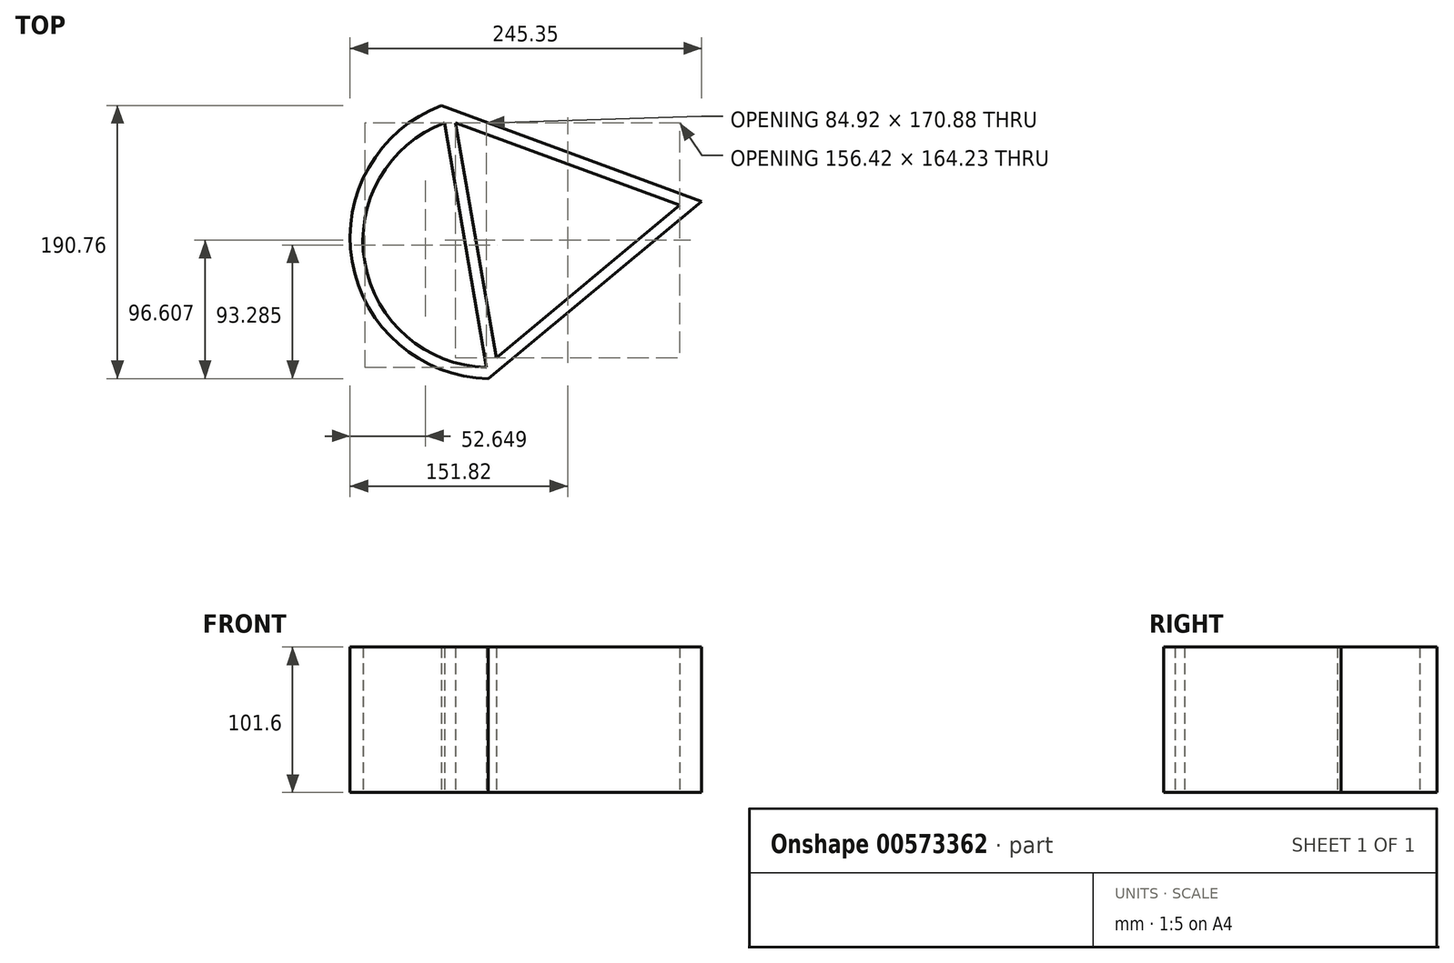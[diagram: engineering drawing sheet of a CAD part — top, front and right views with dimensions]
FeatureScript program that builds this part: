
annotation { "Feature Type Name" : "Feature", "Feature Type Description" : "" }
export const myFeature = defineFeature(function(context is Context, id is Id, definition is map)
    precondition{}
    {
        {
            var Q0;
            Q0=qCreatedBy(makeId("Top.planeOp"),FACE);
            var sketch = newSketch(context, id + "F0", { "sketchPlane" : qUnion([Q0])});
            skCircle(sketch, "E0.cCircle", {"center": v(0, 0) * mm, "radius": 55.87 * mm, "construction": true});
            skLineSegment(sketch, "E0.0", {"start": v(110.14, 18.83) * mm, "end": v(-38.76, -104.8) * mm});
            skLineSegment(sketch, "E0.1", {"start": v(-38.76, -104.8) * mm, "end": v(-71.38, 85.96) * mm});
            skLineSegment(sketch, "E0.2", {"start": v(-71.38, 85.96) * mm, "end": v(110.14, 18.83) * mm});
            skPoint(sketch, "E0.0.midPoint", {"position": v(35.69, -42.98) * mm});
            skCircle(sketch, "E1.cCircle", {"center": v(0, 0) * mm, "radius": 48.11 * mm, "construction": true});
            skLineSegment(sketch, "E1.0", {"start": v(94.82, 16.39) * mm, "end": v(-33.22, -90.3) * mm});
            skLineSegment(sketch, "E1.1", {"start": v(-33.22, -90.3) * mm, "end": v(-61.6, 73.92) * mm});
            skLineSegment(sketch, "E1.2", {"start": v(-61.6, 73.92) * mm, "end": v(94.82, 16.39) * mm});
            skPoint(sketch, "E1.0.midPoint", {"position": v(30.8, -36.96) * mm});
            skArc(sketch, "E2", {"start": v(-71.38, 85.96) * mm, "mid": v(-133.8, -22.88) * mm, "end": v(-38.76, -104.8) * mm});
            skArc(sketch, "E3", {"start": v(-69.32, 73.92) * mm, "mid": v(-125.02, -23.54) * mm, "end": v(-40.1, -96.95) * mm});
            skSolve(sketch);
        }
        {
            var Q0;
            Q0 = qSketchRegion(id + "F0", true);
            extrude(context, id + "F1", {"entities" : qUnion([Q0]), "depth" : 101.6 * mm, "offsetDistance" : 25.4 * mm});
        }
    });
